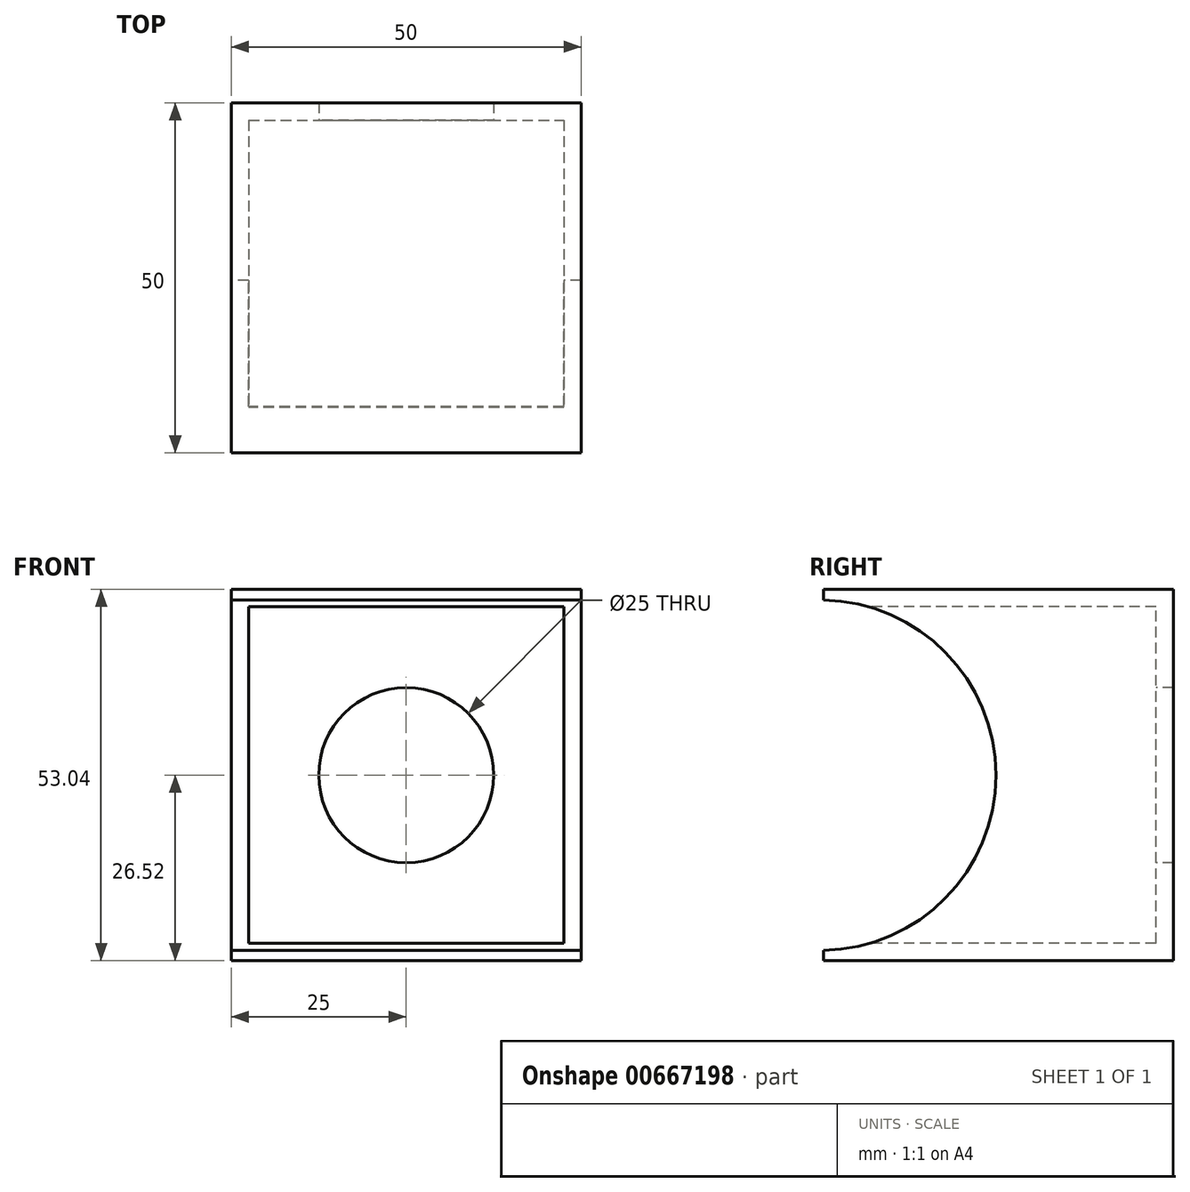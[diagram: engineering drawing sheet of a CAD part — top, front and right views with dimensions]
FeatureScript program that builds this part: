
annotation { "Feature Type Name" : "Feature", "Feature Type Description" : "" }
export const myFeature = defineFeature(function(context is Context, id is Id, definition is map)
    precondition{}
    {
        {
            var Q0;
            Q0=qCreatedBy(makeId("Front.planeOp"),FACE);
            var sketch = newSketch(context, id + "F0", { "sketchPlane" : qUnion([Q0])});
            skLineSegment(sketch, "E0.bottom", {"start": v(-25, -26.52) * mm, "end": v(25, -26.52) * mm});
            skLineSegment(sketch, "E0.top", {"start": v(-25, 26.52) * mm, "end": v(25, 26.52) * mm});
            skLineSegment(sketch, "E0.left", {"start": v(-25, -26.52) * mm, "end": v(-25, 26.52) * mm});
            skLineSegment(sketch, "E0.right", {"start": v(25, -26.52) * mm, "end": v(25, 26.52) * mm});
            skSolve(sketch);
        }
        {
            var Q0;
            Q0=makeQuery(id+"F0.imprint","IMPRINT",FACE,{"disambiguationData":[TD([[makeQuery(id+"F0.imprint","IMPRINT",EDGE,{"derivedFrom":sQuery(id+"F0.wireOp",EDGE,"E0.bottom")}),1.0]])]});
            extrude(context, id + "F1", {"entities" : qUnion([Q0]), "oppositeDirection" : true, "depth" : 50 * mm, "offsetDistance" : 25 * mm});
        }
        {
            var Q0;
            Q0=qCreatedBy(makeId("Right.planeOp"),FACE);
            var sketch = newSketch(context, id + "F2", { "sketchPlane" : qUnion([Q0])});
            skCircle(sketch, "E1", {"center": v(-0.37, -0.02) * mm, "radius": 25 * mm});
            skSolve(sketch);
        }
        {
            var Q0;
            Q0=makeQuery(id+"F2.imprint","IMPRINT",FACE,{"disambiguationData":[TD([[makeQuery(id+"F2.imprint","IMPRINT",EDGE,{"derivedFrom":sQuery(id+"F2.wireOp",EDGE,"E1")}),1.0]])]});
            extrude(context, id + "F3", {"entities" : qUnion([Q0]), "operationType" : NewBodyOperationType.REMOVE, "depth" : 25 * mm, "offsetDistance" : 25 * mm});
        }
        {
            var Q0;
            Q0=makeQuery(id+"F2.imprint","IMPRINT",FACE,{"disambiguationData":[TD([[makeQuery(id+"F2.imprint","IMPRINT",EDGE,{"derivedFrom":sQuery(id+"F2.wireOp",EDGE,"E1")}),1.0]])]});
            extrude(context, id + "F4", {"entities" : qUnion([Q0]), "operationType" : NewBodyOperationType.REMOVE, "oppositeDirection" : true, "depth" : 25 * mm, "offsetDistance" : 25 * mm});
        }
        {
            var Q0;
            {var subQ0=sQuery(id+"F2.wireOp",EDGE,"E1");Q0=makeQuery(id+"F4.boolean.opBoolean","MERGE",FACE,{"derivedFrom":[makeQuery(id+"F3.boolean.opBoolean","COPY",FACE,{"derivedFrom":makeQuery(id+"F3.opExtrude","SWEPT_FACE",FACE,{"disambiguationData":[OSD([subQ0])]})}),makeQuery(id+"F4.opExtrude","SWEPT_FACE",FACE,{"disambiguationData":[OSD([subQ0])]})]});}
            shell(context, id + "F5", {"entities" : qUnion([Q0]), "thickness" : 2.5 * mm});
        }
        {
            var Q0;
            Q0=qCreatedBy(makeId("Front.planeOp"),FACE);
            var sketch = newSketch(context, id + "F6", { "sketchPlane" : qUnion([Q0])});
            skCircle(sketch, "E2", {"center": v(0, 0) * mm, "radius": 12.5 * mm});
            skSolve(sketch);
        }
        {
            var Q0;
            Q0 = qSketchRegion(id + "F6", true);
            extrude(context, id + "F7", {"entities" : qUnion([Q0]), "operationType" : NewBodyOperationType.REMOVE, "oppositeDirection" : true, "depth" : 50 * mm, "offsetDistance" : 25 * mm});
        }
    });
